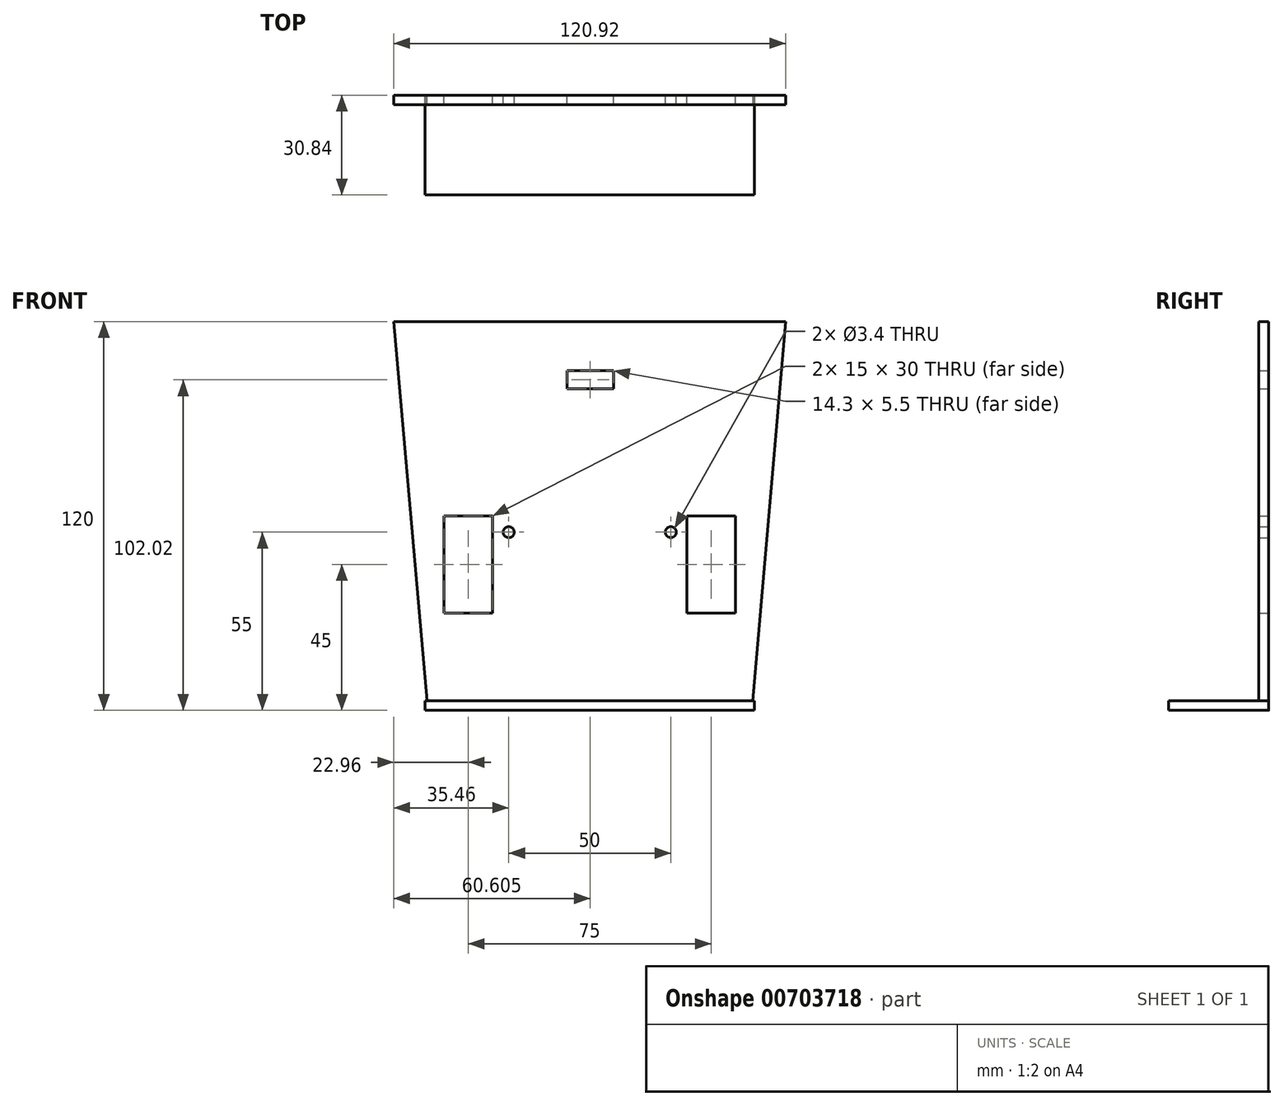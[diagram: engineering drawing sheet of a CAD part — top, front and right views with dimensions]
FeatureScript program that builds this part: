
annotation { "Feature Type Name" : "Feature", "Feature Type Description" : "" }
export const myFeature = defineFeature(function(context is Context, id is Id, definition is map)
    precondition{}
    {
        {
            var Q0;
            Q0=qCreatedBy(makeId("Top.planeOp"),FACE);
            var sketch = newSketch(context, id + "F0", { "sketchPlane" : qUnion([Q0])});
            skLineSegment(sketch, "E0.bottom", {"start": v(0, 0) * mm, "end": v(120, 0) * mm});
            skLineSegment(sketch, "E0.top", {"start": v(0, -40) * mm, "end": v(120, -40) * mm});
            skLineSegment(sketch, "E0.left", {"start": v(0, 0) * mm, "end": v(0, -40) * mm});
            skLineSegment(sketch, "E0.right", {"start": v(120, 0) * mm, "end": v(120, -40) * mm});
            skPoint(sketch, "E1", {"position": v(120, 0) * mm});
            skLineSegment(sketch, "E2", {"start": v(120, 0) * mm, "end": v(120, -47.34) * mm, "construction": true});
            skPoint(sketch, "E3.visualSharp", {"position": v(120, -40) * mm});
            skLineSegment(sketch, "E3.filletArc", {"start": v(120, -40) * mm, "end": v(120, -40) * mm});
            skLineSegment(sketch, "E4.filletArc", {"start": v(120, 0) * mm, "end": v(120, 0) * mm});
            skPoint(sketch, "E5.visualSharp", {"position": v(0, 0) * mm});
            skLineSegment(sketch, "E5.filletArc", {"start": v(0, 0) * mm, "end": v(0, 0) * mm});
            skPoint(sketch, "E6.visualSharp", {"position": v(0, -40) * mm});
            skLineSegment(sketch, "E6.filletArc", {"start": v(0, -40) * mm, "end": v(0, -40) * mm});
            skSolve(sketch);
        }
        {
            var Q0;
            Q0=qSketchRegion(id+"F0",true);
            extrude(context, id + "F1", {"entities" : qUnion([Q0]), "depth" : 130 * mm, "offsetDistance" : 25 * mm, "hasDraft" : true, "draftAngle" : 5 * degree});
        }
        {
            var Q0;
            Q0=qCreatedBy(makeId("Front.planeOp"),FACE);
            var sketch = newSketch(context, id + "F2", { "sketchPlane" : qUnion([Q0])});
            skLineSegment(sketch, "E7.bottom", {"start": v(146.84, 147.54) * mm, "end": v(-36.23, 147.54) * mm});
            skLineSegment(sketch, "E7.top", {"start": v(146.84, -9) * mm, "end": v(-36.23, -9) * mm});
            skLineSegment(sketch, "E7.left", {"start": v(146.84, 147.54) * mm, "end": v(146.84, -9) * mm});
            skLineSegment(sketch, "E7.right", {"start": v(-36.23, 147.54) * mm, "end": v(-36.23, -9) * mm});
            skPoint(sketch, "E7.middle", {"position": v(55.3, 69.27) * mm});
            skSolve(sketch);
        }
        {
            var Q0;
            Q0=makeQuery(id+"F2.imprint","IMPRINT",FACE,{"disambiguationData":[TD([[makeQuery(id+"F2.imprint","IMPRINT",EDGE,{"derivedFrom":sQuery(id+"F2.wireOp",EDGE,"E7.bottom")}),1.0]])]});
            extrude(context, id + "F3", {"entities" : qUnion([Q0]), "operationType" : NewBodyOperationType.REMOVE, "oppositeDirection" : true, "depth" : 150 * mm, "offsetDistance" : 25 * mm});
        }
        {
            var Q0;
            Q0=makeQuery(id+"F1.opExtrude","SWEPT_FACE",FACE,{"disambiguationData":[OSD([sQuery(id+"F0.wireOp",EDGE,"E0.right")])]});
            var Q1;
            Q1=makeQuery(id+"F1.opExtrude","SWEPT_FACE",FACE,{"disambiguationData":[OSD([sQuery(id+"F0.wireOp",EDGE,"E0.left")])]});
            var Q2;
            Q2=makeQuery(id+"F1.opExtrude","CAP_FACE",FACE,{"disambiguationData":[OSD([sQuery(id+"F0.wireOp",EDGE,"E0.bottom"),sQuery(id+"F0.wireOp",EDGE,"E0.top"),sQuery(id+"F0.wireOp",EDGE,"E0.left"),sQuery(id+"F0.wireOp",EDGE,"E0.right")])],"isStart":false});
            var Q3;
            Q3=makeQuery(id+"F1.opExtrude","CAP_EDGE",EDGE,{"disambiguationData":[OSD([sQuery(id+"F0.wireOp",EDGE,"E0.bottom")])],"isStart":true});
            var Q4;
            Q4=makeQuery(id+"F1.opExtrude","SWEPT_FACE",FACE,{"disambiguationData":[OSD([sQuery(id+"F0.wireOp",EDGE,"E0.top")])]});
            fillet(context, id + "F4", {"entities" : qUnion([Q0, Q1, Q2, Q3, Q4]), "radius" : 10 * mm, "tangentPropagation" : true, "allowEdgeOverflow" : false});
        }
        {
            var Q0;
            Q0=makeQuery(id+"F1.opExtrude","SWEPT_FACE",FACE,{"disambiguationData":[OSD([sQuery(id+"F0.wireOp",EDGE,"E0.left")])]});
            var Q1;
            Q1=makeQuery(id+"F4.opFillet","BLEND_FACE",FACE,{"disambiguationData":[OSD([sQuery(id+"F0.wireOp",EDGE,"E0.left"),sQuery(id+"F2.wireOp",EDGE,"E7.bottom"),sQuery(id+"F2.wireOp",EDGE,"E7.top"),sQuery(id+"F2.wireOp",EDGE,"E7.left"),sQuery(id+"F2.wireOp",EDGE,"E7.right")])]});
            var Q2;
            Q2=makeQuery(id+"F4.opFillet","BLEND_FACE",FACE,{"disambiguationData":[OSD([sQuery(id+"F0.wireOp",EDGE,"E0.bottom"),sQuery(id+"F0.wireOp",EDGE,"E0.left")])]});
            var Q3;
            {var subQ0=sQuery(id+"F0.wireOp",EDGE,"E0.left");Q3=makeQuery(id+"F4.opFillet","BLEND_FACE",FACE,{"disambiguationData":[OSD([subQ0]),TDD([makeQuery(id+"F1.opExtrude","CAP_EDGE",EDGE,{"disambiguationData":[OSD([subQ0])],"isStart":true})])]});}
            var Q4;
            {var subQ0=sQuery(id+"F0.wireOp",EDGE,"E0.left");var subQ1=sQuery(id+"F0.wireOp",EDGE,"E0.top");Q4=makeQuery(id+"F4.opFillet","BLEND_FACE",FACE,{"disambiguationData":[OSD([subQ1,subQ0]),TDD([makeQuery(id+"F1.opExtrude","CAP_VERTEX",VERTEX,{"disambiguationData":[OSD([subQ1,subQ0])],"isStart":true})])]});}
            var Q5;
            {var subQ0=sQuery(id+"F0.wireOp",EDGE,"E0.left");var subQ1=sQuery(id+"F0.wireOp",EDGE,"E0.top");Q5=makeQuery(id+"F4.opFillet","BLEND_FACE",FACE,{"disambiguationData":[OSD([subQ1,subQ0]),TDD([makeQuery(id+"F1.opExtrude","SWEPT_EDGE",EDGE,{"disambiguationData":[OSD([subQ1,subQ0])]})])]});}
            var Q6;
            {var subQ0=sQuery(id+"F0.wireOp",EDGE,"E0.top");Q6=makeQuery(id+"F4.opFillet","BLEND_FACE",FACE,{"disambiguationData":[OSD([subQ0]),TDD([makeQuery(id+"F1.opExtrude","CAP_EDGE",EDGE,{"disambiguationData":[OSD([subQ0])],"isStart":true})])]});}
            var Q7;
            Q7=makeQuery(id+"F1.opExtrude","SWEPT_FACE",FACE,{"disambiguationData":[OSD([sQuery(id+"F0.wireOp",EDGE,"E0.top")])]});
            var Q8;
            {var subQ0=sQuery(id+"F0.wireOp",EDGE,"E0.right");var subQ1=sQuery(id+"F0.wireOp",EDGE,"E0.top");Q8=makeQuery(id+"F4.opFillet","BLEND_FACE",FACE,{"disambiguationData":[OSD([subQ1,subQ0]),TDD([makeQuery(id+"F1.opExtrude","SWEPT_EDGE",EDGE,{"disambiguationData":[OSD([subQ1,subQ0])]})])]});}
            var Q9;
            {var subQ0=sQuery(id+"F0.wireOp",EDGE,"E0.right");var subQ1=sQuery(id+"F0.wireOp",EDGE,"E0.top");Q9=makeQuery(id+"F4.opFillet","BLEND_FACE",FACE,{"disambiguationData":[OSD([subQ1,subQ0]),TDD([makeQuery(id+"F1.opExtrude","CAP_VERTEX",VERTEX,{"disambiguationData":[OSD([subQ1,subQ0])],"isStart":true})])]});}
            var Q10;
            {var subQ0=sQuery(id+"F0.wireOp",EDGE,"E0.right");Q10=makeQuery(id+"F4.opFillet","BLEND_FACE",FACE,{"disambiguationData":[OSD([subQ0]),TDD([makeQuery(id+"F1.opExtrude","CAP_EDGE",EDGE,{"disambiguationData":[OSD([subQ0])],"isStart":true})])]});}
            var Q11;
            Q11=makeQuery(id+"F1.opExtrude","SWEPT_FACE",FACE,{"disambiguationData":[OSD([sQuery(id+"F0.wireOp",EDGE,"E0.right")])]});
            var Q12;
            Q12=makeQuery(id+"F4.opFillet","BLEND_FACE",FACE,{"disambiguationData":[OSD([sQuery(id+"F0.wireOp",EDGE,"E0.right"),sQuery(id+"F2.wireOp",EDGE,"E7.bottom"),sQuery(id+"F2.wireOp",EDGE,"E7.top"),sQuery(id+"F2.wireOp",EDGE,"E7.left"),sQuery(id+"F2.wireOp",EDGE,"E7.right")])]});
            var Q13;
            Q13=makeQuery(id+"F4.opFillet","BLEND_FACE",FACE,{"disambiguationData":[OSD([sQuery(id+"F0.wireOp",EDGE,"E0.bottom"),sQuery(id+"F0.wireOp",EDGE,"E0.right")])]});
            var Q14;
            {var subQ0=sQuery(id+"F2.wireOp",EDGE,"E7.right");var subQ1=sQuery(id+"F2.wireOp",EDGE,"E7.left");var subQ2=sQuery(id+"F2.wireOp",EDGE,"E7.top");var subQ3=sQuery(id+"F2.wireOp",EDGE,"E7.bottom");var subQ4=sQuery(id+"F0.wireOp",EDGE,"E0.left");var subQ5=sQuery(id+"F0.wireOp",EDGE,"E0.right");var subQ6=sQuery(id+"F0.wireOp",EDGE,"E0.top");var subQ7=sQuery(id+"F0.wireOp",EDGE,"E0.bottom");Q14=makeQuery(id+"F4.opFillet","BLEND_FACE",FACE,{"disambiguationData":[OSD([subQ7,subQ6,subQ4,subQ5,subQ3,subQ2,subQ1,subQ0]),TDD([makeQuery(id+"F3.boolean.opBoolean","INTERSECT",VERTEX,{"derivedFrom":[makeQuery(id+"F1.opExtrude","CAP_FACE",FACE,{"disambiguationData":[OSD([subQ7,subQ6,subQ4,subQ5])],"isStart":false}),makeQuery(id+"F1.opExtrude","SWEPT_FACE",FACE,{"disambiguationData":[OSD([subQ4])]}),makeQuery(id+"F3.opExtrude","CAP_FACE",FACE,{"disambiguationData":[OSD([subQ3,subQ2,subQ1,subQ0])],"isStart":true})]})])]});}
            var Q15;
            {var subQ0=sQuery(id+"F0.wireOp",EDGE,"E0.left");var subQ1=sQuery(id+"F0.wireOp",EDGE,"E0.top");Q15=makeQuery(id+"F4.opFillet","BLEND_FACE",FACE,{"disambiguationData":[OSD([subQ1,subQ0]),TDD([makeQuery(id+"F1.opExtrude","CAP_VERTEX",VERTEX,{"disambiguationData":[OSD([subQ1,subQ0])],"isStart":false})])]});}
            var Q16;
            {var subQ0=sQuery(id+"F0.wireOp",EDGE,"E0.top");Q16=makeQuery(id+"F4.opFillet","BLEND_FACE",FACE,{"disambiguationData":[OSD([subQ0]),TDD([makeQuery(id+"F1.opExtrude","CAP_EDGE",EDGE,{"disambiguationData":[OSD([subQ0])],"isStart":false})])]});}
            var Q17;
            {var subQ0=sQuery(id+"F0.wireOp",EDGE,"E0.right");var subQ1=sQuery(id+"F0.wireOp",EDGE,"E0.top");Q17=makeQuery(id+"F4.opFillet","BLEND_FACE",FACE,{"disambiguationData":[OSD([subQ1,subQ0]),TDD([makeQuery(id+"F1.opExtrude","CAP_VERTEX",VERTEX,{"disambiguationData":[OSD([subQ1,subQ0])],"isStart":false})])]});}
            var Q18;
            {var subQ0=sQuery(id+"F0.wireOp",EDGE,"E0.right");Q18=makeQuery(id+"F4.opFillet","BLEND_FACE",FACE,{"disambiguationData":[OSD([subQ0]),TDD([makeQuery(id+"F1.opExtrude","CAP_EDGE",EDGE,{"disambiguationData":[OSD([subQ0])],"isStart":false})])]});}
            var Q19;
            {var subQ0=sQuery(id+"F2.wireOp",EDGE,"E7.right");var subQ1=sQuery(id+"F2.wireOp",EDGE,"E7.left");var subQ2=sQuery(id+"F2.wireOp",EDGE,"E7.top");var subQ3=sQuery(id+"F2.wireOp",EDGE,"E7.bottom");var subQ4=sQuery(id+"F0.wireOp",EDGE,"E0.right");var subQ5=sQuery(id+"F0.wireOp",EDGE,"E0.left");var subQ6=sQuery(id+"F0.wireOp",EDGE,"E0.top");var subQ7=sQuery(id+"F0.wireOp",EDGE,"E0.bottom");Q19=makeQuery(id+"F4.opFillet","BLEND_FACE",FACE,{"disambiguationData":[OSD([subQ7,subQ6,subQ5,subQ4,subQ3,subQ2,subQ1,subQ0]),TDD([makeQuery(id+"F3.boolean.opBoolean","INTERSECT",VERTEX,{"derivedFrom":[makeQuery(id+"F1.opExtrude","CAP_FACE",FACE,{"disambiguationData":[OSD([subQ7,subQ6,subQ5,subQ4])],"isStart":false}),makeQuery(id+"F1.opExtrude","SWEPT_FACE",FACE,{"disambiguationData":[OSD([subQ4])]}),makeQuery(id+"F3.opExtrude","CAP_FACE",FACE,{"disambiguationData":[OSD([subQ3,subQ2,subQ1,subQ0])],"isStart":true})]})])]});}
            var Q20;
            {var subQ0=sQuery(id+"F0.wireOp",EDGE,"E0.left");Q20=makeQuery(id+"F4.opFillet","BLEND_FACE",FACE,{"disambiguationData":[OSD([subQ0]),TDD([makeQuery(id+"F1.opExtrude","CAP_EDGE",EDGE,{"disambiguationData":[OSD([subQ0])],"isStart":false})])]});}
            var Q21;
            Q21=makeQuery(id+"F1.opExtrude","CAP_FACE",FACE,{"disambiguationData":[OSD([sQuery(id+"F0.wireOp",EDGE,"E0.bottom"),sQuery(id+"F0.wireOp",EDGE,"E0.top"),sQuery(id+"F0.wireOp",EDGE,"E0.left"),sQuery(id+"F0.wireOp",EDGE,"E0.right")])],"isStart":false});
            var Q22;
            {var subQ0=sQuery(id+"F2.wireOp",EDGE,"E7.right");var subQ1=sQuery(id+"F2.wireOp",EDGE,"E7.left");var subQ2=sQuery(id+"F2.wireOp",EDGE,"E7.top");var subQ3=sQuery(id+"F2.wireOp",EDGE,"E7.bottom");var subQ4=sQuery(id+"F0.wireOp",EDGE,"E0.right");var subQ5=sQuery(id+"F0.wireOp",EDGE,"E0.left");var subQ6=sQuery(id+"F0.wireOp",EDGE,"E0.top");var subQ7=sQuery(id+"F0.wireOp",EDGE,"E0.bottom");Q22=makeQuery(id+"F4.opFillet","BLEND_FACE",FACE,{"disambiguationData":[OSD([subQ7,subQ6,subQ5,subQ4,subQ3,subQ2,subQ1,subQ0]),TDD([makeQuery(id+"F3.boolean.opBoolean","INTERSECT",EDGE,{"derivedFrom":[makeQuery(id+"F1.opExtrude","CAP_FACE",FACE,{"disambiguationData":[OSD([subQ7,subQ6,subQ5,subQ4])],"isStart":false}),makeQuery(id+"F3.opExtrude","CAP_FACE",FACE,{"disambiguationData":[OSD([subQ3,subQ2,subQ1,subQ0])],"isStart":true})]})])]});}
            shell(context, id + "F5", {"entities" : qUnion([Q0, Q1, Q2, Q3, Q4, Q5, Q6, Q7, Q8, Q9, Q10, Q11, Q12, Q13, Q14, Q15, Q16, Q17, Q18, Q19, Q20, Q21, Q22]), "thickness" : 3 * mm});
        }
        {
            var Q0;
            Q0=makeQuery(id+"F3.boolean.opBoolean","COPY",FACE,{"derivedFrom":makeQuery(id+"F3.opExtrude","CAP_FACE",FACE,{"disambiguationData":[OSD([sQuery(id+"F2.wireOp",EDGE,"E7.bottom"),sQuery(id+"F2.wireOp",EDGE,"E7.top"),sQuery(id+"F2.wireOp",EDGE,"E7.left"),sQuery(id+"F2.wireOp",EDGE,"E7.right")])],"isStart":true})});
            var sketch = newSketch(context, id + "F6", { "sketchPlane" : qUnion([Q0])});
            skLineSegment(sketch, "E8.bottom", {"start": v(0, 0) * mm, "end": v(-120, 0) * mm, "construction": true});
            skLineSegment(sketch, "E8.top", {"start": v(-90, 50) * mm, "end": v(-120, 50) * mm, "construction": true});
            skLineSegment(sketch, "E8.left", {"start": v(0, 0) * mm, "end": v(0, 50) * mm, "construction": true});
            skLineSegment(sketch, "E8.right", {"start": v(-120, 0) * mm, "end": v(-120, 50) * mm, "construction": true});
            skLineSegment(sketch, "E9.bottom", {"start": v(-120, 50) * mm, "end": v(-90, 50) * mm, "construction": true});
            skLineSegment(sketch, "E9.top", {"start": v(-120, 60) * mm, "end": v(-90, 60) * mm, "construction": true});
            skLineSegment(sketch, "E9.left", {"start": v(-120, 50) * mm, "end": v(-120, 60) * mm, "construction": true});
            skLineSegment(sketch, "E9.right", {"start": v(-90, 50) * mm, "end": v(-90, 60) * mm, "construction": true});
            skLineSegment(sketch, "E10.top", {"start": v(0, 60) * mm, "end": v(-30, 60) * mm, "construction": true});
            skLineSegment(sketch, "E11", {"start": v(0, 50) * mm, "end": v(0, 60) * mm, "construction": true});
            skLineSegment(sketch, "E12", {"start": v(-30, 60) * mm, "end": v(-30, 50) * mm, "construction": true});
            skLineSegment(sketch, "E13", {"start": v(-90, 50) * mm, "end": v(0, 50) * mm, "construction": true});
            skLineSegment(sketch, "E14.bottom", {"start": v(-30, 60) * mm, "end": v(-15, 60) * mm});
            skLineSegment(sketch, "E14.top", {"start": v(-30, 30) * mm, "end": v(-15, 30) * mm});
            skLineSegment(sketch, "E14.left", {"start": v(-30, 60) * mm, "end": v(-30, 30) * mm});
            skLineSegment(sketch, "E14.right", {"start": v(-15, 60) * mm, "end": v(-15, 30) * mm});
            skLineSegment(sketch, "E15.bottom", {"start": v(-90, 60) * mm, "end": v(-105, 60) * mm});
            skLineSegment(sketch, "E16.top", {"start": v(-90, 30) * mm, "end": v(-105, 30) * mm});
            skLineSegment(sketch, "E16.left", {"start": v(-90, 60) * mm, "end": v(-90, 30) * mm});
            skLineSegment(sketch, "E16.right", {"start": v(-105, 60) * mm, "end": v(-105, 30) * mm});
            skLineSegment(sketch, "E17.bottom", {"start": v(-30, 60) * mm, "end": v(-40, 60) * mm, "construction": true});
            skLineSegment(sketch, "E17.top", {"start": v(-30, 35) * mm, "end": v(-40, 35) * mm, "construction": true});
            skLineSegment(sketch, "E17.left", {"start": v(-30, 60) * mm, "end": v(-30, 35) * mm, "construction": true});
            skLineSegment(sketch, "E17.right", {"start": v(-40, 60) * mm, "end": v(-40, 35) * mm, "construction": true});
            skLineSegment(sketch, "E18.bottom", {"start": v(-90, 60) * mm, "end": v(-80, 60) * mm, "construction": true});
            skLineSegment(sketch, "E18.top", {"start": v(-90, 35) * mm, "end": v(-80, 35) * mm, "construction": true});
            skLineSegment(sketch, "E18.left", {"start": v(-90, 60) * mm, "end": v(-90, 35) * mm, "construction": true});
            skLineSegment(sketch, "E18.right", {"start": v(-80, 60) * mm, "end": v(-80, 35) * mm, "construction": true});
            skLineSegment(sketch, "E19.bottom", {"start": v(-40, 60) * mm, "end": v(-35, 60) * mm, "construction": true});
            skLineSegment(sketch, "E19.top", {"start": v(-40, 55) * mm, "end": v(-35, 55) * mm, "construction": true});
            skLineSegment(sketch, "E19.left", {"start": v(-40, 60) * mm, "end": v(-40, 55) * mm, "construction": true});
            skLineSegment(sketch, "E19.right", {"start": v(-35, 60) * mm, "end": v(-35, 55) * mm, "construction": true});
            skCircle(sketch, "E20", {"center": v(-35, 55) * mm, "radius": 1.7 * mm});
            skLineSegment(sketch, "E21.bottom", {"start": v(-90, 60) * mm, "end": v(-85, 60) * mm, "construction": true});
            skLineSegment(sketch, "E21.top", {"start": v(-90, 55) * mm, "end": v(-85, 55) * mm, "construction": true});
            skLineSegment(sketch, "E21.left", {"start": v(-90, 60) * mm, "end": v(-90, 55) * mm, "construction": true});
            skLineSegment(sketch, "E21.right", {"start": v(-85, 60) * mm, "end": v(-85, 55) * mm, "construction": true});
            skCircle(sketch, "E22", {"center": v(-85, 55) * mm, "radius": 1.7 * mm});
            skLineSegment(sketch, "E23.bottom", {"start": v(-40, 60) * mm, "end": v(-80.3, 60) * mm, "construction": true});
            skLineSegment(sketch, "E23.top", {"start": v(-40, 89.62) * mm, "end": v(-80.3, 89.62) * mm, "construction": true});
            skLineSegment(sketch, "E23.left", {"start": v(-40, 60) * mm, "end": v(-40, 89.62) * mm, "construction": true});
            skLineSegment(sketch, "E23.right", {"start": v(-80.3, 60) * mm, "end": v(-80.3, 89.62) * mm, "construction": true});
            skLineSegment(sketch, "E24.bottom", {"start": v(-80.3, 89.62) * mm, "end": v(-60.15, 89.62) * mm, "construction": true});
            skLineSegment(sketch, "E24.top", {"start": v(-80.3, 102.02) * mm, "end": v(-60.15, 102.02) * mm, "construction": true});
            skLineSegment(sketch, "E24.left", {"start": v(-80.3, 89.62) * mm, "end": v(-80.3, 102.02) * mm, "construction": true});
            skLineSegment(sketch, "E24.right", {"start": v(-60.15, 89.62) * mm, "end": v(-60.15, 102.02) * mm, "construction": true});
            skLineSegment(sketch, "E25.bottom", {"start": v(-67.3, 104.77) * mm, "end": v(-53, 104.77) * mm});
            skLineSegment(sketch, "E25.top", {"start": v(-67.3, 99.27) * mm, "end": v(-53, 99.27) * mm});
            skLineSegment(sketch, "E25.left", {"start": v(-67.3, 104.77) * mm, "end": v(-67.3, 99.27) * mm});
            skLineSegment(sketch, "E25.right", {"start": v(-53, 104.77) * mm, "end": v(-53, 99.27) * mm});
            skPoint(sketch, "E25.middle", {"position": v(-60.15, 102.02) * mm});
            skSolve(sketch);
        }
        {
            var Q0;
            Q0=makeQuery(id+"F6.imprint","IMPRINT",FACE,{"disambiguationData":[TD([[makeQuery(id+"F6.imprint","IMPRINT",EDGE,{"derivedFrom":sQuery(id+"F6.wireOp",EDGE,"E14.bottom")}),-1.0]])]});
            var Q1;
            Q1=makeQuery(id+"F6.imprint","IMPRINT",FACE,{"disambiguationData":[TD([[makeQuery(id+"F6.imprint","IMPRINT",EDGE,{"derivedFrom":sQuery(id+"F6.wireOp",EDGE,"E15.bottom")}),1.0]])]});
            var Q2;
            Q2=makeQuery(id+"F6.imprint","IMPRINT",FACE,{"disambiguationData":[TD([[makeQuery(id+"F6.imprint","IMPRINT",EDGE,{"derivedFrom":sQuery(id+"F6.wireOp",EDGE,"E20")}),1.0]])]});
            var Q3;
            Q3=makeQuery(id+"F6.imprint","IMPRINT",FACE,{"disambiguationData":[TD([[makeQuery(id+"F6.imprint","IMPRINT",EDGE,{"derivedFrom":sQuery(id+"F6.wireOp",EDGE,"E22")}),1.0]])]});
            var Q4;
            Q4=makeQuery(id+"F6.imprint","IMPRINT",FACE,{"disambiguationData":[TD([[makeQuery(id+"F6.imprint","IMPRINT",EDGE,{"derivedFrom":sQuery(id+"F6.wireOp",EDGE,"E25.bottom")}),-1.0]])]});
            extrude(context, id + "F7", {"entities" : qUnion([Q0, Q1, Q2, Q3, Q4]), "operationType" : NewBodyOperationType.REMOVE, "oppositeDirection" : true, "depth" : 29.25 * mm, "offsetDistance" : 25 * mm});
        }
    });
